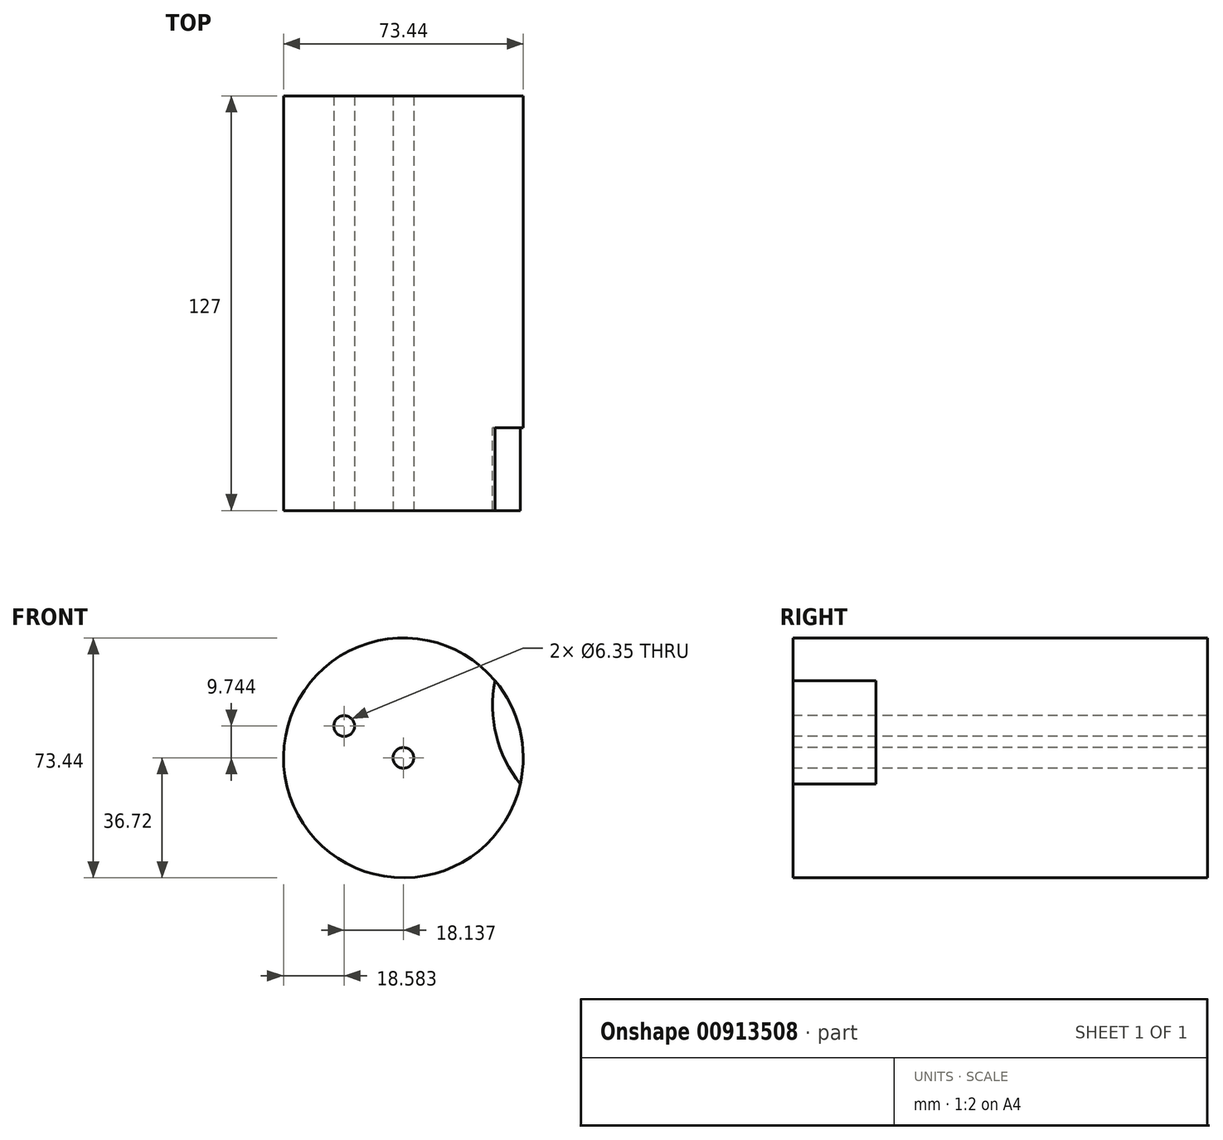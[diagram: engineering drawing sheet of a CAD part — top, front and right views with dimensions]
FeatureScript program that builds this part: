
annotation { "Feature Type Name" : "Feature", "Feature Type Description" : "" }
export const myFeature = defineFeature(function(context is Context, id is Id, definition is map)
    precondition{}
    {
        {
            var Q0;
            Q0=qCreatedBy(makeId("Front.planeOp"),FACE);
            var sketch = newSketch(context, id + "F0", { "sketchPlane" : qUnion([Q0])});
            skCircle(sketch, "E0", {"center": v(0, 0) * mm, "radius": 36.72 * mm});
            skSolve(sketch);
        }
        {
            var Q0;
            Q0 = qSketchRegion(id + "F0", true);
            extrude(context, id + "F1", {"entities" : qUnion([Q0]), "depth" : 127 * mm, "offsetDistance" : 25.4 * mm});
        }
        {
            var Q0;
            Q0=qCreatedBy(makeId("Front.planeOp"),FACE);
            cPlane(context, id + "F2", {"entities" : qUnion([Q0]), "cplaneType" : CPlaneType.OFFSET, "offset" : 101.6 * mm, "width" : 152.4 * mm, "height" : 152.4 * mm});
        }
        {
            var Q0;
            Q0=qCreatedBy(id+"F2.planeOp",FACE);
            var sketch = newSketch(context, id + "F3", { "sketchPlane" : qUnion([Q0])});
            skCircle(sketch, "E1", {"center": v(65.84, 16.08) * mm, "radius": 38.47 * mm});
            skSolve(sketch);
        }
        {
            var Q0;
            Q0 = qSketchRegion(id + "F3", true);
            extrude(context, id + "F4", {"entities" : qUnion([Q0]), "operationType" : NewBodyOperationType.REMOVE, "depth" : 62.74 * mm, "offsetDistance" : 25.4 * mm});
        }
        {
            var Q0;
            Q0=makeQuery(id+"F1.opExtrude","CAP_FACE",FACE,{"disambiguationData":[OSD([sQuery(id+"F0.wireOp",EDGE,"E0")])],"isStart":false});
            var sketch = newSketch(context, id + "F5", { "sketchPlane" : qUnion([Q0])});
            skPoint(sketch, "E2", {"position": v(-18.14, 9.74) * mm});
            skPoint(sketch, "E3", {"position": v(0, 0) * mm});
            skSolve(sketch);
        }
        {
            var Q0;
            Q0=sQuery(id+"F5.wireOp",VERTEX,"E2");
            var Q1;
            Q1=sQuery(id+"F5.wireOp",VERTEX,"E3");
            var Q2;
            Q2=makeQuery(id+"F1.opExtrude","SWEPT_BODY",BODY,{"disambiguationData":[OSD([sQuery(id+"F0.wireOp",EDGE,"E0")])]});
            hole(context, id + "F6", {"style" : HoleStyle.SIMPLE, "endStyle" : HoleEndStyle.THROUGH, "holeDiameter" : 6.35 * mm, "majorDiameter" : 6.35 * mm, "isTappedThrough" : true, "tappedDepth" : 12.7 * mm, "tapClearance" : 3, "locations" : qUnion([Q0, Q1]), "scope" : qUnion([Q2])});
        }
    });
